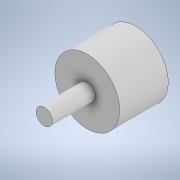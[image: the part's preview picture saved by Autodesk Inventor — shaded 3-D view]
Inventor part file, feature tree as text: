
AUTODESK INVENTOR PART (.ipt)
format: ipt  version: 2021 (Build 250183000, 183)  size: 125,440 bytes
history: native  units: mm
features: sketch x5, extrude x3, loft x1
ambient origin geometry x8: Origin, YZ Plane, XZ Plane, XY Plane, X Axis, Y Axis, Z Axis, Center Point
bodies: Body1 (feature_tree)
feature tree (9):
  extrude  "Extrusion4"  Depth=7.0mm TaperAngle=0.0deg
  loft  "Loft3"
  extrude  "Extrusion5"  Depth=2.5mm
  extrude  "Extrusion6"  Depth=6.0mm
  sketch  "Sketch8"  dims[d35=12.0mm d36=7.0mm d37=0.0mm]
  sketch  "Sketch9"  dims[d38=5.0mm d39=5.0mm]
  sketch  "Sketch10"  dims[d40=2.5mm d41=2.5mm]
  sketch  "Sketch11"  dims[d42=6.0mm d43=6.0mm]
  sketch  "Sketch12"  dims[d44=3.0mm d45=3.0mm d46=0.0mm d47=90.0deg d48=0.0mm d49=90.0deg d50=2.0mm d51=0.0mm d52=3.0mm d53=8.0mm d54=0.0mm d22=0.5mm d23=0.872665mm d24=0.5mm d25=0.872665mm]
